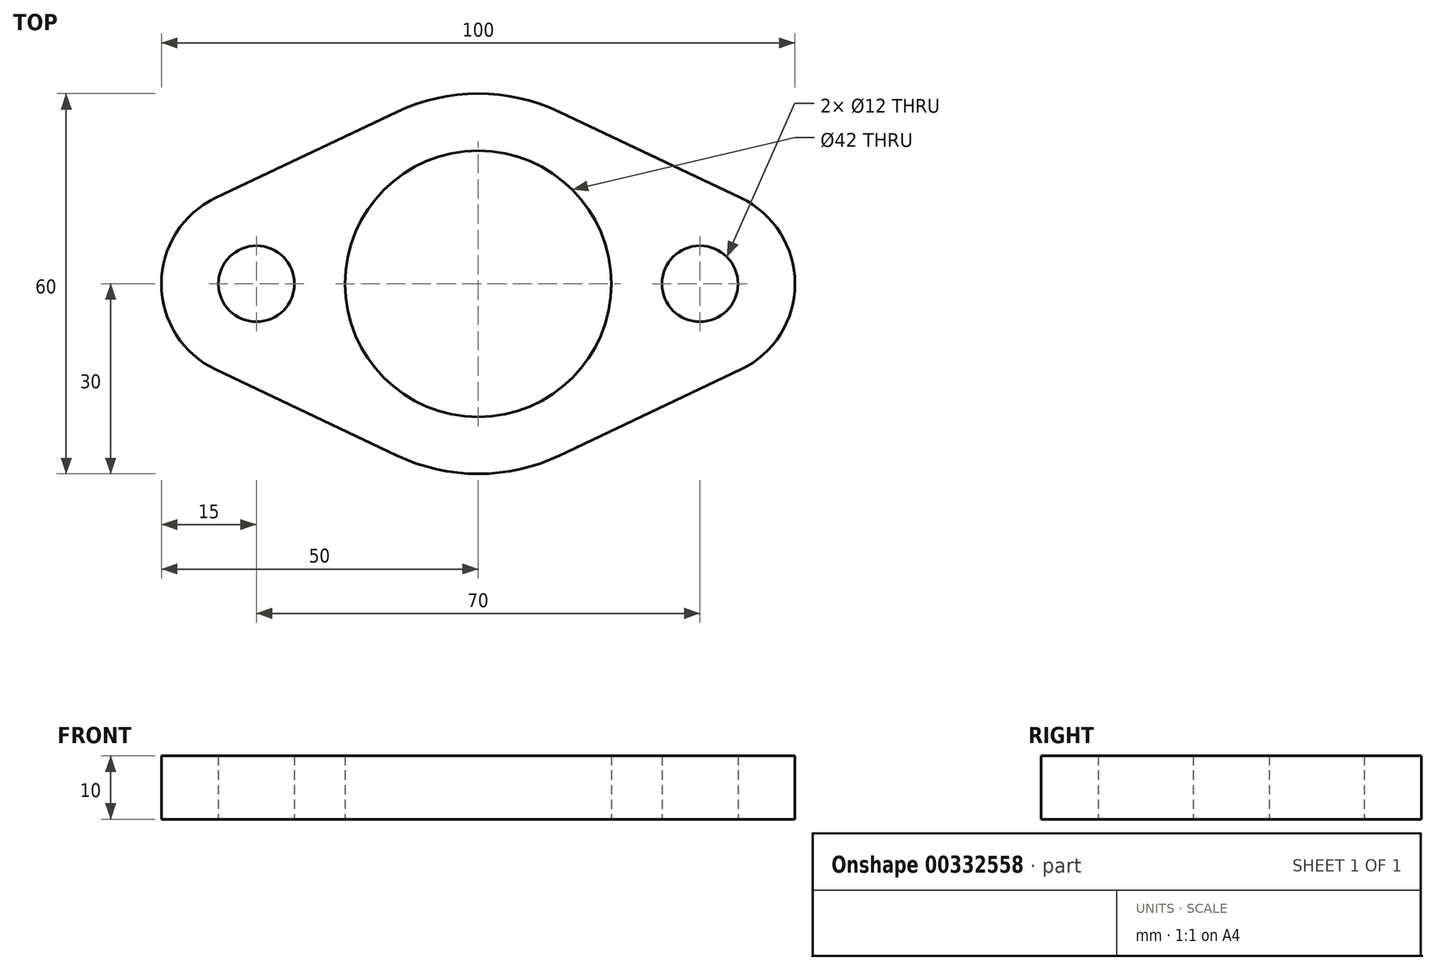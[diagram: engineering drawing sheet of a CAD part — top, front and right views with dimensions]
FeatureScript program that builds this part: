
annotation { "Feature Type Name" : "Feature", "Feature Type Description" : "" }
export const myFeature = defineFeature(function(context is Context, id is Id, definition is map)
    precondition{}
    {
        {
            var Q0;
            Q0=qCreatedBy(makeId("Top.planeOp"),FACE);
            var sketch = newSketch(context, id + "F0", { "sketchPlane" : qUnion([Q0])});
            skArc(sketch, "E0", {"start": v(12.86, 27.1) * mm, "mid": v(0, 30) * mm, "end": v(-12.86, 27.1) * mm});
            skCircle(sketch, "E1", {"center": v(0, 0) * mm, "radius": 21 * mm});
            skCircle(sketch, "E2", {"center": v(35, 0) * mm, "radius": 6 * mm});
            skCircle(sketch, "E3", {"center": v(-35, 0) * mm, "radius": 6 * mm});
            skArc(sketch, "E4", {"start": v(-41.43, 13.55) * mm, "mid": v(-50, 0) * mm, "end": v(-41.43, -13.55) * mm});
            skLineSegment(sketch, "E5", {"start": v(-41.43, 13.55) * mm, "end": v(-12.86, 27.1) * mm});
            skLineSegment(sketch, "E6.MirrorCS", {"start": v(-41.43, -13.55) * mm, "end": v(-12.86, -27.1) * mm});
            skLineSegment(sketch, "E7.MirrorCS", {"start": v(41.43, 13.55) * mm, "end": v(12.86, 27.1) * mm});
            skLineSegment(sketch, "E8.MirrorCS", {"start": v(41.43, -13.55) * mm, "end": v(12.86, -27.1) * mm});
            skArc(sketch, "E9.trimOffspring", {"start": v(41.43, -13.55) * mm, "mid": v(50, 0) * mm, "end": v(41.43, 13.55) * mm});
            skArc(sketch, "E10.trimOffspring", {"start": v(-12.86, -27.1) * mm, "mid": v(0, -30) * mm, "end": v(12.86, -27.1) * mm});
            skSolve(sketch);
        }
        {
            var Q0;
            Q0=makeQuery(id+"F0.imprint","IMPRINT",FACE,{"disambiguationData":[TD([[makeQuery(id+"F0.imprint","IMPRINT",EDGE,{"derivedFrom":sQuery(id+"F0.wireOp",EDGE,"E0")}),1.0]])]});
            extrude(context, id + "F1", {"entities" : qUnion([Q0]), "depth" : 10 * mm});
        }
    });
